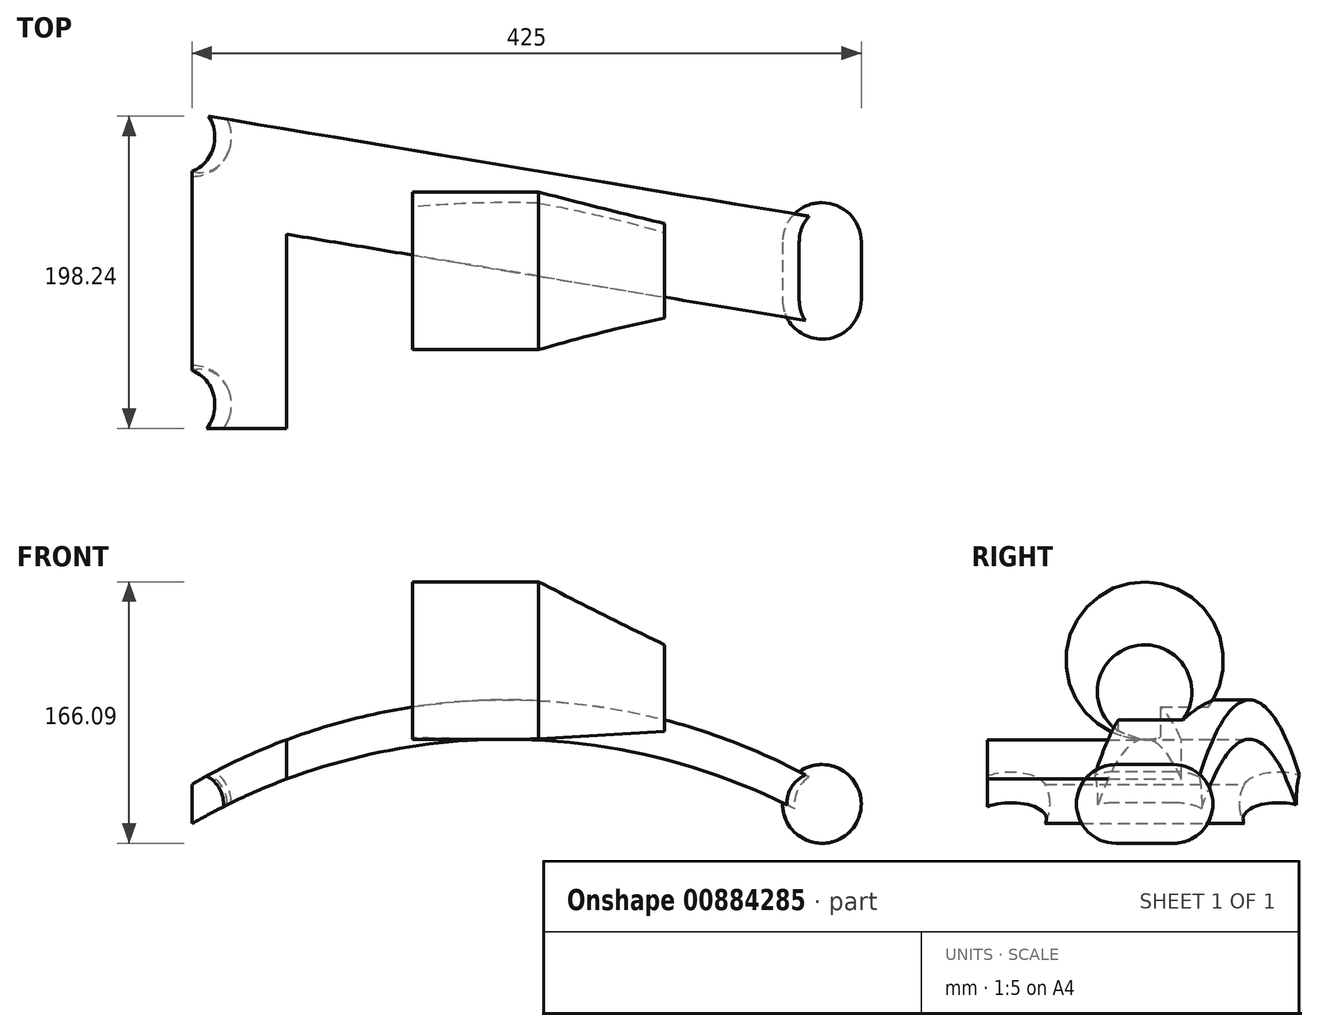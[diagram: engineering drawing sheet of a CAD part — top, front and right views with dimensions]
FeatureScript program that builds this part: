
annotation { "Feature Type Name" : "Feature", "Feature Type Description" : "" }
export const myFeature = defineFeature(function(context is Context, id is Id, definition is map)
    precondition{}
    {
        {
            var Q0;
            Q0=qCreatedBy(makeId("Front.planeOp"),FACE);
            var sketch = newSketch(context, id + "F0", { "sketchPlane" : qUnion([Q0])});
            skLineSegment(sketch, "E0", {"start": v(-200, -12.5) * mm, "end": v(-200, 12.5) * mm});
            skArc(sketch, "E1", {"start": v(-200, 12.5) * mm, "mid": v(0, 66.09) * mm, "end": v(200, 12.5) * mm});
            skLineSegment(sketch, "E2", {"start": v(200, 12.5) * mm, "end": v(200, -12.5) * mm});
            skArc(sketch, "E3", {"start": v(-200, -12.5) * mm, "mid": v(0, 41.09) * mm, "end": v(200, -12.5) * mm});
            skPoint(sketch, "E4", {"position": v(-200, 0) * mm});
            skPoint(sketch, "E5", {"position": v(0, 66.09) * mm});
            skSolve(sketch);
        }
        {
            var Q0;
            Q0=makeQuery(id+"F0.imprint","IMPRINT",FACE,{"disambiguationData":[TD([[makeQuery(id+"F0.imprint","IMPRINT",EDGE,{"derivedFrom":sQuery(id+"F0.wireOp",EDGE,"E0")}),-1.0]])]});
            extrude(context, id + "F1", {"entities" : qUnion([Q0]), "endBound" : BoundingType.SYMMETRIC, "depth" : 200 * mm, "offsetDistance" : 25 * mm});
        }
        {
            var Q0;
            Q0=qCreatedBy(makeId("Top.planeOp"),FACE);
            var sketch = newSketch(context, id + "F2", { "sketchPlane" : qUnion([Q0])});
            skLineSegment(sketch, "E6", {"start": v(-200, -100) * mm, "end": v(-200, 100) * mm});
            skLineSegment(sketch, "E7", {"start": v(-200, 100) * mm, "end": v(200, 33.33) * mm});
            skLineSegment(sketch, "E8", {"start": v(200, 33.33) * mm, "end": v(200, -33.33) * mm});
            skLineSegment(sketch, "E9", {"start": v(200, -33.33) * mm, "end": v(-140, 23.33) * mm});
            skLineSegment(sketch, "E10", {"start": v(-140, 23.33) * mm, "end": v(-140, -100) * mm});
            skLineSegment(sketch, "E11", {"start": v(-140, -100) * mm, "end": v(-200, -100) * mm});
            skPoint(sketch, "E12", {"position": v(-200, 0) * mm});
            skLineSegment(sketch, "E13", {"start": v(-200, 100) * mm, "end": v(200, 100) * mm});
            skLineSegment(sketch, "E14", {"start": v(200, 100) * mm, "end": v(200, 33.33) * mm});
            skLineSegment(sketch, "E15", {"start": v(-140, -100) * mm, "end": v(200, -100) * mm});
            skLineSegment(sketch, "E16", {"start": v(200, -100) * mm, "end": v(200, -33.33) * mm});
            skPoint(sketch, "E17", {"position": v(200, 0) * mm});
            skSolve(sketch);
        }
        {
            var Q0;
            Q0=makeQuery(id+"F2.imprint","IMPRINT",FACE,{"disambiguationData":[TD([[makeQuery(id+"F2.imprint","IMPRINT",EDGE,{"derivedFrom":sQuery(id+"F2.wireOp",EDGE,"E9")}),1.0]])]});
            var Q1;
            Q1=makeQuery(id+"F2.imprint","IMPRINT",FACE,{"disambiguationData":[TD([[makeQuery(id+"F2.imprint","IMPRINT",EDGE,{"derivedFrom":sQuery(id+"F2.wireOp",EDGE,"E7")}),1.0]])]});
            extrude(context, id + "F3", {"entities" : qUnion([Q0, Q1]), "operationType" : NewBodyOperationType.REMOVE, "endBound" : BoundingType.THROUGH_ALL, "oppositeDirection" : true, "depth" : 25 * mm, "offsetDistance" : 25 * mm, "hasSecondDirection" : true, "secondDirectionBound" : SecondDirectionBoundingType.THROUGH_ALL, "secondDirectionOppositeDirection" : false, "secondDirectionDepth" : 25 * mm});
        }
        {
            var Q0;
            Q0=makeQuery(id+"F1.opExtrude","SWEPT_FACE",FACE,{"disambiguationData":[OSD([sQuery(id+"F0.wireOp",EDGE,"E0")])]});
            var sketch = newSketch(context, id + "F4", { "sketchPlane" : qUnion([Q0])});
            skArc(sketch, "E18", {"start": v(-110, 0) * mm, "mid": v(-85, 25) * mm, "end": v(-60, 0) * mm});
            skArc(sketch, "E19", {"start": v(60, 0) * mm, "mid": v(85, 25) * mm, "end": v(110, 0) * mm});
            skLineSegment(sketch, "E20", {"start": v(-110, 0) * mm, "end": v(-60, 0) * mm});
            skLineSegment(sketch, "E21", {"start": v(60, 0) * mm, "end": v(110, 0) * mm});
            skSolve(sketch);
        }
        {
            var Q0;
            Q0 = qSketchRegion(id + "F4", true);
            var Q1;
            Q1=sQuery(id+"F4.wireOp",EDGE,"E20");
            revolve(context, id + "F5", {"operationType" : NewBodyOperationType.ADD, "surfaceOperationType" : NewSurfaceOperationType.NEW, "entities" : qUnion([Q0]), "axis" : qUnion([Q1]), "revolveType" : RevolveType.FULL});
        }
        {
            var Q0;
            Q0=makeQuery(id+"F1.opExtrude","SWEPT_FACE",FACE,{"disambiguationData":[OSD([sQuery(id+"F0.wireOp",EDGE,"E2")])]});
            var sketch = newSketch(context, id + "F6", { "sketchPlane" : qUnion([Q0])});
            skLineSegment(sketch, "E22", {"start": v(-18.33, 25) * mm, "end": v(18.33, 25) * mm});
            skArc(sketch, "E23", {"start": v(-43.33, 0) * mm, "mid": v(-36.01, 17.68) * mm, "end": v(-18.33, 25) * mm});
            skPoint(sketch, "E23.startSnap0", {"position": v(-33.33, 0) * mm});
            skArc(sketch, "E24", {"start": v(18.33, 25) * mm, "mid": v(36.01, 17.68) * mm, "end": v(43.33, 0) * mm});
            skLineSegment(sketch, "E25", {"start": v(-43.33, 0) * mm, "end": v(43.33, 0) * mm});
            skSolve(sketch);
        }
        {
            var Q0;
            Q0 = qSketchRegion(id + "F6", true);
            var Q1;
            Q1=sQuery(id+"F6.wireOp",EDGE,"E25");
            revolve(context, id + "F7", {"operationType" : NewBodyOperationType.ADD, "surfaceOperationType" : NewSurfaceOperationType.NEW, "entities" : qUnion([Q0]), "axis" : qUnion([Q1]), "revolveType" : RevolveType.FULL});
        }
        {
            var Q0;
            Q0=qCreatedBy(makeId("Front.planeOp"),FACE);
            var sketch = newSketch(context, id + "F8", { "sketchPlane" : qUnion([Q0])});
            skLineSegment(sketch, "E26", {"start": v(20, 91.09) * mm, "end": v(-60, 91.09) * mm});
            skLineSegment(sketch, "E27", {"start": v(-60, 91.09) * mm, "end": v(-60, 141.09) * mm});
            skLineSegment(sketch, "E28", {"start": v(-60, 141.09) * mm, "end": v(20, 141.09) * mm});
            skLineSegment(sketch, "E29", {"start": v(20, 141.09) * mm, "end": v(20, 91.09) * mm});
            skSolve(sketch);
        }
        {
            var Q0;
            Q0 = qSketchRegion(id + "F8", true);
            var Q1;
            Q1=sQuery(id+"F8.wireOp",EDGE,"E26");
            revolve(context, id + "F9", {"operationType" : NewBodyOperationType.ADD, "surfaceOperationType" : NewSurfaceOperationType.NEW, "entities" : qUnion([Q0]), "axis" : qUnion([Q1]), "revolveType" : RevolveType.FULL});
        }
        {
            var Q0;
            Q0=qCreatedBy(makeId("Right.planeOp"),FACE);
            cPlane(context, id + "F10", {"entities" : qUnion([Q0]), "cplaneType" : CPlaneType.OFFSET, "offset" : 100 * mm, "width" : 150 * mm, "height" : 150 * mm});
        }
        {
            var Q0;
            Q0=qCreatedBy(id+"F10.planeOp",FACE);
            var sketch = newSketch(context, id + "F11", { "sketchPlane" : qUnion([Q0])});
            skCircle(sketch, "E30", {"center": v(0, 71.09) * mm, "radius": 30 * mm});
            skPoint(sketch, "E31", {"position": v(30, 71.09) * mm});
            skPoint(sketch, "E32", {"position": v(-30, 71.09) * mm});
            skLineSegment(sketch, "E33", {"start": v(-16.67, 46.15) * mm, "end": v(-16.67, 53.39) * mm});
            skLineSegment(sketch, "E34", {"start": v(-16.67, 53.39) * mm, "end": v(24.22, 53.39) * mm});
            skSolve(sketch);
        }
        {
            var Q0;
            Q0=makeQuery(id+"F9.opRevolve","SWEPT_FACE",FACE,{"disambiguationData":[OSD([sQuery(id+"F8.wireOp",EDGE,"E29")])]});
            var sketch = newSketch(context, id + "F12", { "sketchPlane" : qUnion([Q0])});
            skPoint(sketch, "E35", {"position": v(0, 91.09) * mm});
            skPoint(sketch, "E36", {"position": v(50, 91.09) * mm});
            skPoint(sketch, "E37", {"position": v(-50, 91.09) * mm});
            skSolve(sketch);
        }
        {
            var Q1;
            {var subQ0=sQuery(id+"F8.wireOp",EDGE,"E29");Q1=makeQuery(id+"F12.imprint","IMPRINT",FACE,{"disambiguationData":[TD([[makeQuery(id+"F12.imprint","IMPRINT",EDGE,{"derivedFrom":makeQuery(id+"F9.opRevolve","SWEPT_EDGE",EDGE,{"disambiguationData":[OSD([sQuery(id+"F8.wireOp",EDGE,"E28"),subQ0])]})}),1.0]])]});}
            var Q2;
            {var subQ0=sQuery(id+"F11.wireOp",EDGE,"E33");Q2=makeQuery(id+"F11.imprint","IMPRINT",FACE,{"disambiguationData":[TD([[makeQuery(id+"F11.imprint","IMPRINT",EDGE,{"derivedFrom":subQ0}),1.0]])]});}
            loft(context, id + "F13", {"operationType" : NewBodyOperationType.ADD, "sheetProfilesArray" : [{ "sheetProfileEntities" : qUnion([Q1]) }, { "sheetProfileEntities" : qUnion([Q2]) }]});
        }
    });
